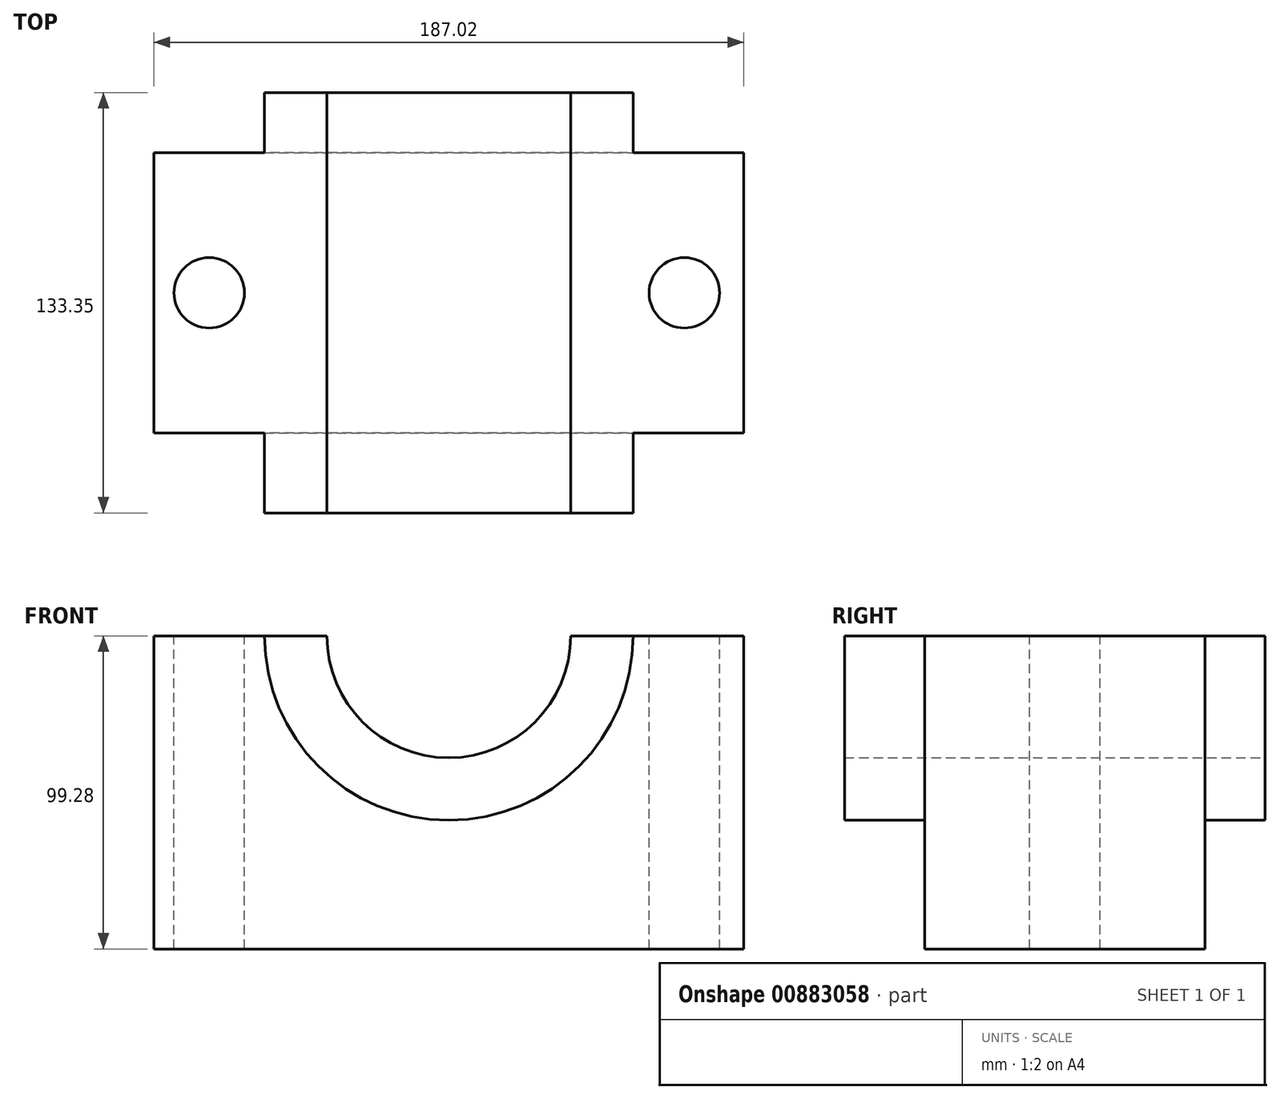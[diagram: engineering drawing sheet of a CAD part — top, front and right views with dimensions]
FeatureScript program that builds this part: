
annotation { "Feature Type Name" : "Feature", "Feature Type Description" : "" }
export const myFeature = defineFeature(function(context is Context, id is Id, definition is map)
    precondition{}
    {
        {
            var Q0;
            Q0=qCreatedBy(makeId("Front.planeOp"),FACE);
            var sketch = newSketch(context, id + "F0", { "sketchPlane" : qUnion([Q0])});
            skLineSegment(sketch, "E0.bottom", {"start": v(93.5, 49.64) * mm, "end": v(58.46, 49.64) * mm});
            skLineSegment(sketch, "E0.top", {"start": v(93.5, -49.64) * mm, "end": v(-93.5, -49.64) * mm});
            skLineSegment(sketch, "E0.left", {"start": v(93.5, 49.64) * mm, "end": v(93.5, -49.64) * mm});
            skLineSegment(sketch, "E0.right", {"start": v(-93.5, 49.64) * mm, "end": v(-93.5, -49.64) * mm});
            skPoint(sketch, "E0.middle", {"position": v(0, 0) * mm});
            skArc(sketch, "E1", {"start": v(-58.46, 49.64) * mm, "mid": v(0, -8.82) * mm, "end": v(58.46, 49.64) * mm});
            skLineSegment(sketch, "E2.trimOffspring", {"start": v(-58.46, 49.64) * mm, "end": v(-93.5, 49.64) * mm});
            skSolve(sketch);
        }
        {
            var Q0;
            Q0=makeQuery(id+"F0.imprint","IMPRINT",FACE,{"disambiguationData":[TD([[makeQuery(id+"F0.imprint","IMPRINT",EDGE,{"derivedFrom":sQuery(id+"F0.wireOp",EDGE,"E0.bottom")}),1.0]])]});
            extrude(context, id + "F1", {"entities" : qUnion([Q0]), "depth" : 88.9 * mm, "offsetDistance" : 25.4 * mm});
        }
        {
            var Q0;
            Q0=makeQuery(id+"F1.opExtrude","CAP_FACE",FACE,{"disambiguationData":[OSD([sQuery(id+"F0.wireOp",EDGE,"E0.bottom"),sQuery(id+"F0.wireOp",EDGE,"E0.top"),sQuery(id+"F0.wireOp",EDGE,"E0.left"),sQuery(id+"F0.wireOp",EDGE,"E0.right"),sQuery(id+"F0.wireOp",EDGE,"E1"),sQuery(id+"F0.wireOp",EDGE,"E2.trimOffspring")])],"isStart":false});
            var sketch = newSketch(context, id + "F2", { "sketchPlane" : qUnion([Q0])});
            skArc(sketch, "E3", {"start": v(-58.46, 49.64) * mm, "mid": v(0, -8.82) * mm, "end": v(58.46, 49.64) * mm});
            skArc(sketch, "E4", {"start": v(-38.64, 49.64) * mm, "mid": v(0, 11) * mm, "end": v(38.64, 49.64) * mm});
            skLineSegment(sketch, "E5", {"start": v(-58.46, 49.64) * mm, "end": v(-38.64, 49.64) * mm});
            skLineSegment(sketch, "E6.trimOffspring", {"start": v(38.64, 49.64) * mm, "end": v(58.46, 49.64) * mm});
            skSolve(sketch);
        }
        {
            var Q0;
            Q0 = qSketchRegion(id + "F2", true);
            extrude(context, id + "F3", {"entities" : qUnion([Q0]), "operationType" : NewBodyOperationType.ADD, "depth" : 25.4 * mm, "offsetDistance" : 25.4 * mm, "hasSecondDirection" : true, "secondDirectionOppositeDirection" : true, "secondDirectionDepth" : 107.95 * mm});
        }
        {
            var Q0;
            Q0=makeQuery(id+"F3.boolean.opBoolean","MERGE",FACE,{"derivedFrom":[makeQuery(id+"F1.opExtrude","SWEPT_FACE",FACE,{"disambiguationData":[OSD([sQuery(id+"F0.wireOp",EDGE,"E2.trimOffspring")])]}),makeQuery(id+"F3.opExtrude","SWEPT_FACE",FACE,{"disambiguationData":[OSD([sQuery(id+"F2.wireOp",EDGE,"E5")])]})]});
            var sketch = newSketch(context, id + "F4", { "sketchPlane" : qUnion([Q0])});
            skCircle(sketch, "E7", {"center": v(-75.98, -44.45) * mm, "radius": 11.18 * mm});
            skPoint(sketch, "E7.centerSnap0", {"position": v(-93.5, -44.45) * mm});
            skPoint(sketch, "E7.centerSnap1", {"position": v(-75.98, -88.9) * mm});
            skCircle(sketch, "E8", {"center": v(74.7, -44.45) * mm, "radius": 11.18 * mm});
            skSolve(sketch);
        }
        {
            var Q0;
            Q0 = qSketchRegion(id + "F4", true);
            extrude(context, id + "F5", {"entities" : qUnion([Q0]), "operationType" : NewBodyOperationType.REMOVE, "endBound" : BoundingType.UP_TO_NEXT, "oppositeDirection" : true, "depth" : 25.4 * mm, "offsetDistance" : 25.4 * mm});
        }
    });
